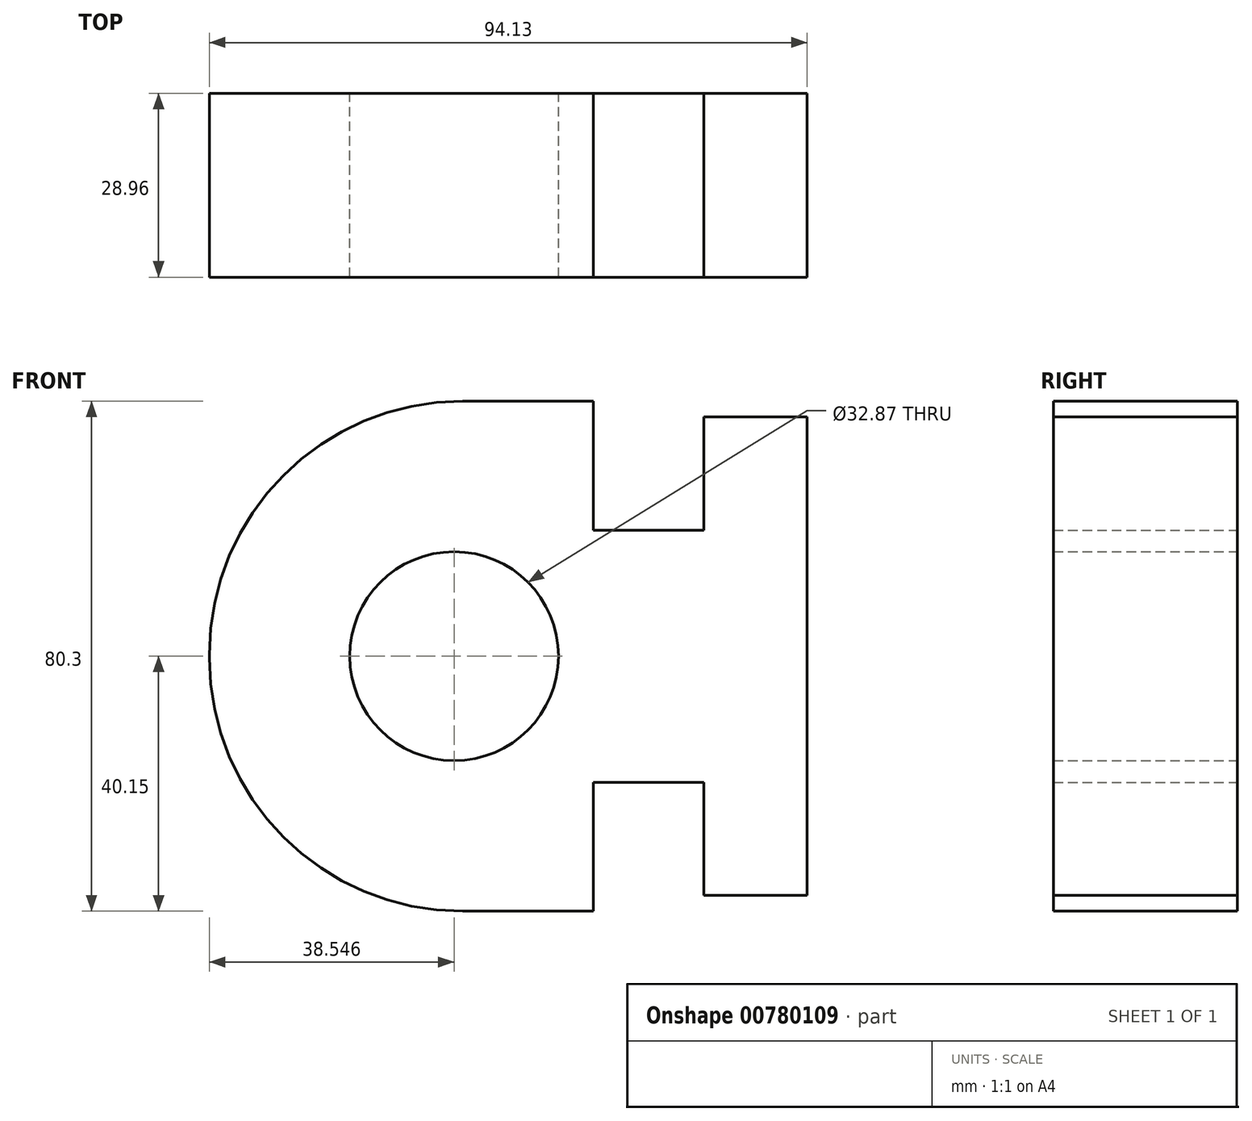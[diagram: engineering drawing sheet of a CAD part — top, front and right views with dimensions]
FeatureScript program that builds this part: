
annotation { "Feature Type Name" : "Feature", "Feature Type Description" : "" }
export const myFeature = defineFeature(function(context is Context, id is Id, definition is map)
    precondition{}
    {
        {
            var Q0;
            Q0=qCreatedBy(makeId("Front.planeOp"),FACE);
            var sketch = newSketch(context, id + "F0", { "sketchPlane" : qUnion([Q0])});
            skLineSegment(sketch, "E0", {"start": v(0, 37.67) * mm, "end": v(-16.27, 37.67) * mm});
            skLineSegment(sketch, "E1", {"start": v(-16.27, 36.78) * mm, "end": v(-16.27, 19.84) * mm});
            skLineSegment(sketch, "E2", {"start": v(-16.27, 19.84) * mm, "end": v(-33.66, 19.84) * mm});
            skLineSegment(sketch, "E3", {"start": v(-33.66, 19.84) * mm, "end": v(-33.66, 40.15) * mm});
            skLineSegment(sketch, "E4", {"start": v(-33.66, 40.15) * mm, "end": v(-55.5, 40.15) * mm});
            skLineSegment(sketch, "E5", {"start": v(0, 37.67) * mm, "end": v(0, 0) * mm});
            skLineSegment(sketch, "E6", {"start": v(-55.5, 40.15) * mm, "end": v(-65.2, 40.15) * mm});
            skLineSegment(sketch, "E7", {"start": v(-65.2, 40.15) * mm, "end": v(-94.13, 40.15) * mm});
            skLineSegment(sketch, "E8", {"start": v(-94.13, 40.15) * mm, "end": v(-94.13, 0) * mm});
            skLineSegment(sketch, "E9", {"start": v(-94.13, 0) * mm, "end": v(0, 0) * mm});
            skLineSegment(sketch, "E10.MirrorCS", {"start": v(0, -37.67) * mm, "end": v(0, 0) * mm});
            skLineSegment(sketch, "E11.MirrorCS", {"start": v(0, -37.67) * mm, "end": v(-16.27, -37.67) * mm});
            skLineSegment(sketch, "E12.MirrorCS", {"start": v(-16.27, -36.78) * mm, "end": v(-16.27, -19.84) * mm});
            skLineSegment(sketch, "E13.MirrorCS", {"start": v(-16.27, -19.84) * mm, "end": v(-33.66, -19.84) * mm});
            skLineSegment(sketch, "E14.MirrorCS", {"start": v(-33.66, -19.84) * mm, "end": v(-33.66, -40.15) * mm});
            skLineSegment(sketch, "E15.MirrorCS", {"start": v(-33.66, -40.15) * mm, "end": v(-55.5, -40.15) * mm});
            skLineSegment(sketch, "E16.MirrorCS", {"start": v(-55.5, -40.15) * mm, "end": v(-65.2, -40.15) * mm});
            skLineSegment(sketch, "E17.MirrorCS", {"start": v(-65.2, -40.15) * mm, "end": v(-94.13, -40.15) * mm});
            skLineSegment(sketch, "E18.MirrorCS", {"start": v(-94.13, -40.15) * mm, "end": v(-94.13, 0) * mm});
            skLineSegment(sketch, "E19", {"start": v(-16.27, 37.67) * mm, "end": v(-16.27, 36.78) * mm});
            skLineSegment(sketch, "E20", {"start": v(-16.27, -36.78) * mm, "end": v(-16.27, -37.67) * mm});
            skCircle(sketch, "E21", {"center": v(-55.58, 0) * mm, "radius": 16.44 * mm});
            skSolve(sketch);
        }
        {
            var Q0;
            {var subQ4=sQuery(id+"F0.wireOp",EDGE,"E10.MirrorCS");Q0=makeQuery(id+"F0.imprint","IMPRINT",FACE,{"disambiguationData":[TD([[makeQuery(id+"F0.imprint","IMPRINT",EDGE,{"derivedFrom":subQ4}),1.0]])]});}
            var Q1;
            Q1=makeQuery(id+"F0.imprint","IMPRINT",FACE,{"disambiguationData":[TD([[makeQuery(id+"F0.imprint","IMPRINT",EDGE,{"derivedFrom":sQuery(id+"F0.wireOp",EDGE,"E0")}),1.0]])]});
            extrude(context, id + "F1", {"entities" : qUnion([Q0, Q1]), "depth" : 28.96 * mm, "offsetDistance" : 25.4 * mm});
        }
        {
            var Q0;
            Q0=makeQuery(id+"F1.opExtrude","SWEPT_EDGE",EDGE,{"disambiguationData":[OSD([sQuery(id+"F0.wireOp",EDGE,"E7"),sQuery(id+"F0.wireOp",EDGE,"E8")])]});
            var Q1;
            Q1=makeQuery(id+"F1.opExtrude","SWEPT_EDGE",EDGE,{"disambiguationData":[OSD([sQuery(id+"F0.wireOp",EDGE,"E17.MirrorCS"),sQuery(id+"F0.wireOp",EDGE,"E18.MirrorCS")])]});
            fillet(context, id + "F2", {"entities" : qUnion([Q0, Q1]), "radius" : 39.86 * mm, "tangentPropagation" : true, "allowEdgeOverflow" : false});
        }
    });
